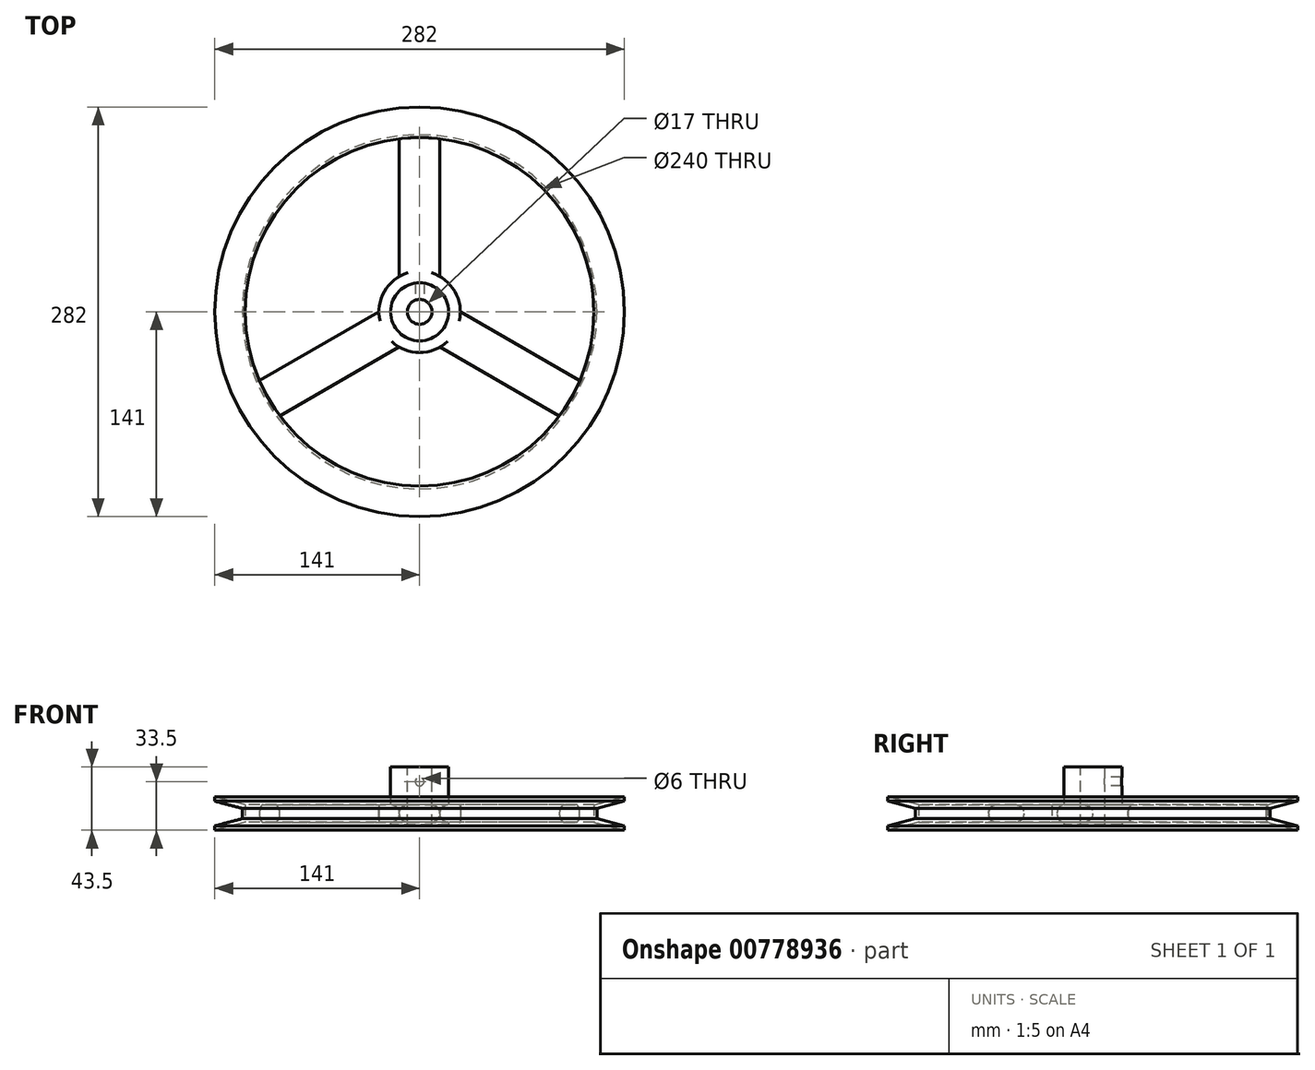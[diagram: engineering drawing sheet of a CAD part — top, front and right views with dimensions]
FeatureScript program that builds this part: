
annotation { "Feature Type Name" : "Feature", "Feature Type Description" : "" }
export const myFeature = defineFeature(function(context is Context, id is Id, definition is map)
    precondition{}
    {
        {
            var Q0;
            Q0=qCreatedBy(makeId("Top.planeOp"),FACE);
            var sketch = newSketch(context, id + "F0", { "sketchPlane" : qUnion([Q0])});
            skCircle(sketch, "E0", {"center": v(0, 0) * mm, "radius": 120 * mm});
            skCircle(sketch, "E1", {"center": v(0, 0) * mm, "radius": 141 * mm});
            skSolve(sketch);
        }
        {
            var Q0;
            Q0 = qSketchRegion(id + "F0", true);
            extrude(context, id + "F1", {"entities" : qUnion([Q0]), "endBound" : BoundingType.SYMMETRIC, "depth" : 23 * mm, "offsetDistance" : 25 * mm});
        }
        {
            var Q0;
            Q0=qCreatedBy(makeId("Right.planeOp"),FACE);
            var sketch = newSketch(context, id + "F2", { "sketchPlane" : qUnion([Q0])});
            skLineSegment(sketch, "E2", {"start": v(0, 0) * mm, "end": v(0, 56.48) * mm, "construction": true});
            skLineSegment(sketch, "E3", {"start": v(-141, 8.5) * mm, "end": v(-122, 3.5) * mm});
            skLineSegment(sketch, "E4", {"start": v(-122, 3.5) * mm, "end": v(-122, -3.5) * mm});
            skLineSegment(sketch, "E5", {"start": v(-122, -3.5) * mm, "end": v(-141, -8.5) * mm});
            skLineSegment(sketch, "E6", {"start": v(-141, 8.5) * mm, "end": v(-141, -8.5) * mm});
            skSolve(sketch);
        }
        {
            var Q0;
            Q0 = qSketchRegion(id + "F2", true);
            var Q1;
            Q1=sQuery(id+"F2.wireOp",EDGE,"E2");
            revolve(context, id + "F3", {"operationType" : NewBodyOperationType.REMOVE, "surfaceOperationType" : NewSurfaceOperationType.NEW, "entities" : qUnion([Q0]), "axis" : qUnion([Q1]), "revolveType" : RevolveType.FULL});
        }
        {
            var Q0;
            Q0=qCreatedBy(makeId("Right.planeOp"),FACE);
            var sketch = newSketch(context, id + "F4", { "sketchPlane" : qUnion([Q0])});
            skPoint(sketch, "E7", {"position": v(-120, 6) * mm});
            skLineSegment(sketch, "E8", {"start": v(-120, 6) * mm, "end": v(-141, 11.5) * mm});
            skLineSegment(sketch, "E9", {"start": v(-141, 11.5) * mm, "end": v(-120, 11.5) * mm});
            skLineSegment(sketch, "E10", {"start": v(-120, 11.5) * mm, "end": v(-120, 6) * mm});
            skLineSegment(sketch, "E11", {"start": v(0, 0) * mm, "end": v(0, 58) * mm, "construction": true});
            skLineSegment(sketch, "E12", {"start": v(0, 0) * mm, "end": v(-38.36, 0) * mm, "construction": true});
            skLineSegment(sketch, "E13.MirrorCS", {"start": v(-141, -11.5) * mm, "end": v(-120, -11.5) * mm});
            skLineSegment(sketch, "E14.MirrorCS", {"start": v(-120, -6) * mm, "end": v(-141, -11.5) * mm});
            skLineSegment(sketch, "E15.MirrorCS", {"start": v(-120, -11.5) * mm, "end": v(-120, -6) * mm});
            skSolve(sketch);
        }
        {
            var Q0;
            Q0 = qSketchRegion(id + "F4", true);
            var Q1;
            Q1=sQuery(id+"F4.wireOp",EDGE,"E11");
            revolve(context, id + "F5", {"operationType" : NewBodyOperationType.REMOVE, "surfaceOperationType" : NewSurfaceOperationType.NEW, "entities" : qUnion([Q0]), "axis" : qUnion([Q1]), "revolveType" : RevolveType.FULL, "oppositeDirection" : true});
        }
        {
            var Q0;
            Q0=qCreatedBy(makeId("Top.planeOp"),FACE);
            var sketch = newSketch(context, id + "F6", { "sketchPlane" : qUnion([Q0])});
            skArc(sketch, "E16", {"start": v(-14, 24.25) * mm, "mid": v(-24.25, 14) * mm, "end": v(-28, 0) * mm});
            skLineSegment(sketch, "E17", {"start": v(0, 0) * mm, "end": v(0, 127.93) * mm, "construction": true});
            skArc(sketch, "E18.0", {"start": v(14, 119.18) * mm, "mid": v(0, 120) * mm, "end": v(-14, 119.18) * mm});
            skLineSegment(sketch, "E19", {"start": v(-14, 119.18) * mm, "end": v(-14, 24.25) * mm});
            skLineSegment(sketch, "E20", {"start": v(14, 119.18) * mm, "end": v(14, 24.25) * mm});
            skLineSegment(sketch, "E21.1.0", {"start": v(-96.21, -71.71) * mm, "end": v(-14, -24.25) * mm});
            skLineSegment(sketch, "E21.1.1", {"start": v(-110.21, -47.47) * mm, "end": v(-28, 0) * mm});
            skLineSegment(sketch, "E21.2.0", {"start": v(110.21, -47.47) * mm, "end": v(28, 0) * mm});
            skLineSegment(sketch, "E21.2.1", {"start": v(96.21, -71.71) * mm, "end": v(14, -24.25) * mm});
            skArc(sketch, "E22.0", {"start": v(-110.21, -47.47) * mm, "mid": v(-103.92, -60) * mm, "end": v(-96.21, -71.71) * mm});
            skArc(sketch, "E23.trimOffspring", {"start": v(96.21, -71.71) * mm, "mid": v(103.92, -60) * mm, "end": v(110.21, -47.47) * mm});
            skArc(sketch, "E24.trimOffspring", {"start": v(-14, -24.25) * mm, "mid": v(0, -28) * mm, "end": v(14, -24.25) * mm});
            skArc(sketch, "E25.trimOffspring", {"start": v(28, 0) * mm, "mid": v(24.25, 14) * mm, "end": v(14, 24.25) * mm});
            skSolve(sketch);
        }
        {
            var Q0;
            Q0 = qSketchRegion(id + "F6", true);
            extrude(context, id + "F7", {"entities" : qUnion([Q0]), "endBound" : BoundingType.SYMMETRIC, "depth" : 12 * mm, "offsetDistance" : 25 * mm});
        }
        {
            var Q0;
            Q0=makeQuery(id+"F7.opExtrude","CAP_FACE",FACE,{"disambiguationData":[OSD([sQuery(id+"F6.wireOp",EDGE,"E16")])],"isStart":false});
            var sketch = newSketch(context, id + "F8", { "sketchPlane" : qUnion([Q0])});
            skCircle(sketch, "E26", {"center": v(0, 0) * mm, "radius": 20 * mm});
            skSolve(sketch);
        }
        {
            var Q0;
            Q0 = qSketchRegion(id + "F8", true);
            extrude(context, id + "F9", {"entities" : qUnion([Q0]), "operationType" : NewBodyOperationType.ADD, "depth" : 26 * mm, "offsetDistance" : 25 * mm, "hasSecondDirection" : true, "secondDirectionOppositeDirection" : true, "secondDirectionDepth" : 14 * mm});
        }
        {
            var Q0;
            Q0=makeQuery(id+"F9.opExtrude","CAP_FACE",FACE,{"disambiguationData":[OSD([sQuery(id+"F8.wireOp",EDGE,"E26")])],"isStart":false});
            var sketch = newSketch(context, id + "F10", { "sketchPlane" : qUnion([Q0])});
            skCircle(sketch, "E27", {"center": v(0, 0) * mm, "radius": 8.5 * mm});
            skSolve(sketch);
        }
        {
            var Q0;
            Q0 = qSketchRegion(id + "F10", true);
            extrude(context, id + "F11", {"entities" : qUnion([Q0]), "operationType" : NewBodyOperationType.REMOVE, "endBound" : BoundingType.THROUGH_ALL, "oppositeDirection" : true, "depth" : 25 * mm, "offsetDistance" : 25 * mm});
        }
        {
            var Q0;
            Q0=makeQuery(id+"F7.opExtrude","CAP_EDGE",EDGE,{"disambiguationData":[OSD([sQuery(id+"F6.wireOp",EDGE,"E19")])],"isStart":false});
            var Q1;
            Q1=makeQuery(id+"F7.opExtrude","CAP_EDGE",EDGE,{"disambiguationData":[OSD([sQuery(id+"F6.wireOp",EDGE,"E19")])],"isStart":true});
            var Q2;
            Q2=makeQuery(id+"F7.opExtrude","CAP_EDGE",EDGE,{"disambiguationData":[OSD([sQuery(id+"F6.wireOp",EDGE,"E20")])],"isStart":false});
            var Q3;
            Q3=makeQuery(id+"F7.opExtrude","CAP_EDGE",EDGE,{"disambiguationData":[OSD([sQuery(id+"F6.wireOp",EDGE,"E20")])],"isStart":true});
            var Q4;
            Q4=makeQuery(id+"F7.opExtrude","CAP_EDGE",EDGE,{"disambiguationData":[OSD([sQuery(id+"F6.wireOp",EDGE,"E21.2.0")])],"isStart":true});
            var Q5;
            Q5=makeQuery(id+"F7.opExtrude","CAP_EDGE",EDGE,{"disambiguationData":[OSD([sQuery(id+"F6.wireOp",EDGE,"E21.2.0")])],"isStart":false});
            var Q6;
            Q6=makeQuery(id+"F7.opExtrude","CAP_EDGE",EDGE,{"disambiguationData":[OSD([sQuery(id+"F6.wireOp",EDGE,"E21.2.1")])],"isStart":false});
            var Q7;
            Q7=makeQuery(id+"F7.opExtrude","CAP_EDGE",EDGE,{"disambiguationData":[OSD([sQuery(id+"F6.wireOp",EDGE,"E21.2.1")])],"isStart":true});
            var Q8;
            Q8=makeQuery(id+"F7.opExtrude","CAP_EDGE",EDGE,{"disambiguationData":[OSD([sQuery(id+"F6.wireOp",EDGE,"E21.1.0")])],"isStart":false});
            var Q9;
            Q9=makeQuery(id+"F7.opExtrude","CAP_EDGE",EDGE,{"disambiguationData":[OSD([sQuery(id+"F6.wireOp",EDGE,"E21.1.0")])],"isStart":true});
            var Q10;
            Q10=makeQuery(id+"F7.opExtrude","CAP_EDGE",EDGE,{"disambiguationData":[OSD([sQuery(id+"F6.wireOp",EDGE,"E21.1.1")])],"isStart":false});
            var Q11;
            Q11=makeQuery(id+"F7.opExtrude","CAP_EDGE",EDGE,{"disambiguationData":[OSD([sQuery(id+"F6.wireOp",EDGE,"E21.1.1")])],"isStart":true});
            fillet(context, id + "F12", {"entities" : qUnion([Q0, Q1, Q2, Q3, Q4, Q5, Q6, Q7, Q8, Q9, Q10, Q11]), "radius" : 6 * mm, "tangentPropagation" : true, "allowEdgeOverflow" : false});
        }
        {
            var Q0;
            Q0=qCreatedBy(makeId("Front.planeOp"),FACE);
            var sketch = newSketch(context, id + "F13", { "sketchPlane" : qUnion([Q0])});
            skCircle(sketch, "E28", {"center": v(0, 22) * mm, "radius": 3 * mm});
            skSolve(sketch);
        }
        {
            var Q0;
            Q0 = qSketchRegion(id + "F13", true);
            extrude(context, id + "F14", {"entities" : qUnion([Q0]), "operationType" : NewBodyOperationType.REMOVE, "endBound" : BoundingType.THROUGH_ALL, "oppositeDirection" : true, "depth" : 25 * mm, "offsetDistance" : 25 * mm});
        }
    });
